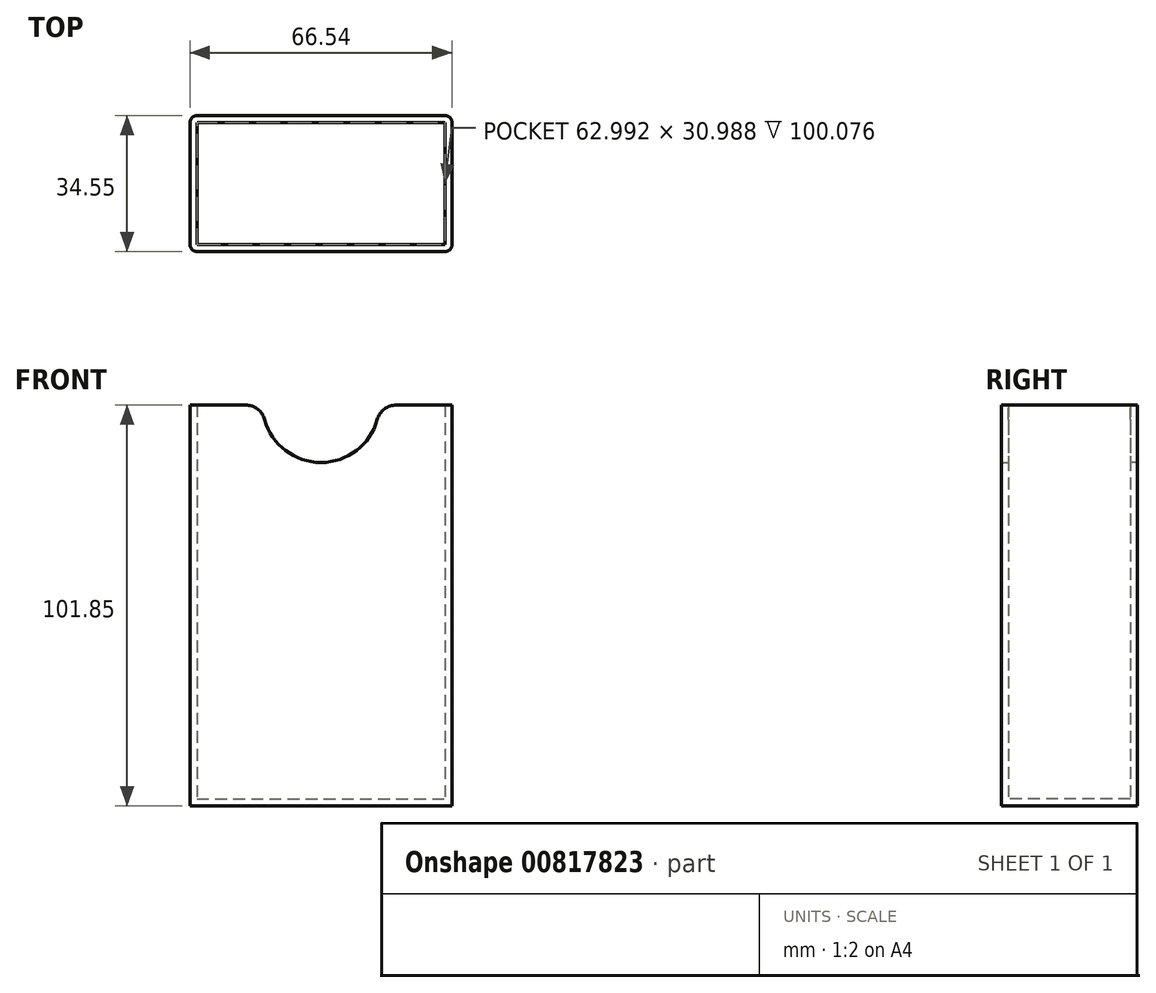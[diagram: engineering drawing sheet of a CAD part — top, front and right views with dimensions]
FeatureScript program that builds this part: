
annotation { "Feature Type Name" : "Feature", "Feature Type Description" : "" }
export const myFeature = defineFeature(function(context is Context, id is Id, definition is map)
    precondition{}
    {
        {
            var Q0;
            Q0=qCreatedBy(makeId("Top.planeOp"),FACE);
            var sketch = newSketch(context, id + "F0", { "sketchPlane" : qUnion([Q0])});
            skLineSegment(sketch, "E0.bottom", {"start": v(-33.27, 23.9) * mm, "end": v(33.27, 23.9) * mm});
            skLineSegment(sketch, "E0.top", {"start": v(-33.27, -10.65) * mm, "end": v(33.27, -10.65) * mm});
            skLineSegment(sketch, "E0.left", {"start": v(-33.27, 23.9) * mm, "end": v(-33.27, -10.65) * mm});
            skLineSegment(sketch, "E0.right", {"start": v(33.27, 23.9) * mm, "end": v(33.27, -10.65) * mm});
            skSolve(sketch);
        }
        {
            var Q0;
            Q0=makeQuery(id+"F0.imprint","IMPRINT",FACE,{"disambiguationData":[TD([[makeQuery(id+"F0.imprint","IMPRINT",EDGE,{"derivedFrom":sQuery(id+"F0.wireOp",EDGE,"E0.bottom")}),-1.0]])]});
            extrude(context, id + "F1", {"entities" : qUnion([Q0]), "depth" : 101.85 * mm, "offsetDistance" : 25.4 * mm});
        }
        {
            var Q0;
            Q0=makeQuery(id+"F1.opExtrude","CAP_FACE",FACE,{"disambiguationData":[OSD([sQuery(id+"F0.wireOp",EDGE,"E0.bottom"),sQuery(id+"F0.wireOp",EDGE,"E0.top"),sQuery(id+"F0.wireOp",EDGE,"E0.left"),sQuery(id+"F0.wireOp",EDGE,"E0.right")])],"isStart":false});
            var Q1;
            Q1=makeQuery(id+"F1.opExtrude","SWEPT_BODY",BODY,{"disambiguationData":[OSD([sQuery(id+"F0.wireOp",EDGE,"E0.bottom"),sQuery(id+"F0.wireOp",EDGE,"E0.top"),sQuery(id+"F0.wireOp",EDGE,"E0.left"),sQuery(id+"F0.wireOp",EDGE,"E0.right")])]});
            shell(context, id + "F2", {"entities" : qUnion([Q0]), "parts" : qUnion([Q1]), "thickness" : 1.78 * mm});
        }
        {
            var Q0;
            Q0=makeQuery(id+"F1.opExtrude","SWEPT_EDGE",EDGE,{"disambiguationData":[OSD([sQuery(id+"F0.wireOp",EDGE,"E0.bottom"),sQuery(id+"F0.wireOp",EDGE,"E0.left")])]});
            var Q1;
            Q1=makeQuery(id+"F1.opExtrude","SWEPT_EDGE",EDGE,{"disambiguationData":[OSD([sQuery(id+"F0.wireOp",EDGE,"E0.top"),sQuery(id+"F0.wireOp",EDGE,"E0.left")])]});
            var Q2;
            Q2=makeQuery(id+"F1.opExtrude","SWEPT_EDGE",EDGE,{"disambiguationData":[OSD([sQuery(id+"F0.wireOp",EDGE,"E0.top"),sQuery(id+"F0.wireOp",EDGE,"E0.right")])]});
            var Q3;
            Q3=makeQuery(id+"F1.opExtrude","SWEPT_EDGE",EDGE,{"disambiguationData":[OSD([sQuery(id+"F0.wireOp",EDGE,"E0.bottom"),sQuery(id+"F0.wireOp",EDGE,"E0.right")])]});
            fillet(context, id + "F3", {"entities" : qUnion([Q0, Q1, Q2, Q3]), "radius" : 1.78 * mm, "tangentPropagation" : true, "allowEdgeOverflow" : false});
        }
        {
            var Q0;
            Q0=qCreatedBy(makeId("Front.planeOp"),FACE);
            var sketch = newSketch(context, id + "F4", { "sketchPlane" : qUnion([Q0])});
            skCircle(sketch, "E1", {"center": v(0, 102.1) * mm, "radius": 14.84 * mm});
            skSolve(sketch);
        }
        {
            var Q0;
            Q0=makeQuery(id+"F4.imprint","IMPRINT",FACE,{"disambiguationData":[TD([[makeQuery(id+"F4.imprint","IMPRINT",EDGE,{"derivedFrom":sQuery(id+"F4.wireOp",EDGE,"E1")}),1.0]])]});
            extrude(context, id + "F5", {"entities" : qUnion([Q0]), "operationType" : NewBodyOperationType.REMOVE, "endBound" : BoundingType.THROUGH_ALL, "oppositeDirection" : true, "depth" : 25.4 * mm, "offsetDistance" : 25.4 * mm});
        }
        {
            var Q0;
            Q0 = qSketchRegion(id + "F4", true);
            extrude(context, id + "F6", {"entities" : qUnion([Q0]), "operationType" : NewBodyOperationType.REMOVE, "depth" : 25.4 * mm, "offsetDistance" : 25.4 * mm});
        }
        {
            var Q0;
            Q0=makeQuery(id+"F5.boolean.opBoolean","INTERSECT",EDGE,{"disambiguationData":[OD(0.0)],"derivedFrom":[makeQuery(id+"F1.opExtrude","CAP_FACE",FACE,{"disambiguationData":[OSD([sQuery(id+"F0.wireOp",EDGE,"E0.bottom"),sQuery(id+"F0.wireOp",EDGE,"E0.top"),sQuery(id+"F0.wireOp",EDGE,"E0.left"),sQuery(id+"F0.wireOp",EDGE,"E0.right")])],"isStart":false}),makeQuery(id+"F5.opExtrude","SWEPT_FACE",FACE,{"disambiguationData":[OSD([sQuery(id+"F4.wireOp",EDGE,"E1")])]})]});
            var Q1;
            Q1=makeQuery(id+"F6.boolean.opBoolean","INTERSECT",EDGE,{"disambiguationData":[OD(0.0)],"derivedFrom":[makeQuery(id+"F1.opExtrude","CAP_FACE",FACE,{"disambiguationData":[OSD([sQuery(id+"F0.wireOp",EDGE,"E0.bottom"),sQuery(id+"F0.wireOp",EDGE,"E0.top"),sQuery(id+"F0.wireOp",EDGE,"E0.left"),sQuery(id+"F0.wireOp",EDGE,"E0.right")])],"isStart":false}),makeQuery(id+"F6.opExtrude","SWEPT_FACE",FACE,{"disambiguationData":[OSD([sQuery(id+"F4.wireOp",EDGE,"E1")])]})]});
            var Q2;
            Q2=makeQuery(id+"F5.boolean.opBoolean","INTERSECT",EDGE,{"disambiguationData":[OD(1.0)],"derivedFrom":[makeQuery(id+"F1.opExtrude","CAP_FACE",FACE,{"disambiguationData":[OSD([sQuery(id+"F0.wireOp",EDGE,"E0.bottom"),sQuery(id+"F0.wireOp",EDGE,"E0.top"),sQuery(id+"F0.wireOp",EDGE,"E0.left"),sQuery(id+"F0.wireOp",EDGE,"E0.right")])],"isStart":false}),makeQuery(id+"F5.opExtrude","SWEPT_FACE",FACE,{"disambiguationData":[OSD([sQuery(id+"F4.wireOp",EDGE,"E1")])]})]});
            var Q3;
            Q3=makeQuery(id+"F6.boolean.opBoolean","INTERSECT",EDGE,{"disambiguationData":[OD(1.0)],"derivedFrom":[makeQuery(id+"F1.opExtrude","CAP_FACE",FACE,{"disambiguationData":[OSD([sQuery(id+"F0.wireOp",EDGE,"E0.bottom"),sQuery(id+"F0.wireOp",EDGE,"E0.top"),sQuery(id+"F0.wireOp",EDGE,"E0.left"),sQuery(id+"F0.wireOp",EDGE,"E0.right")])],"isStart":false}),makeQuery(id+"F6.opExtrude","SWEPT_FACE",FACE,{"disambiguationData":[OSD([sQuery(id+"F4.wireOp",EDGE,"E1")])]})]});
            fillet(context, id + "F7", {"entities" : qUnion([Q0, Q1, Q2, Q3]), "radius" : 5.08 * mm, "tangentPropagation" : true, "allowEdgeOverflow" : false});
        }
    });
